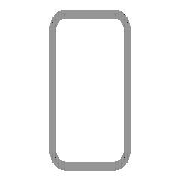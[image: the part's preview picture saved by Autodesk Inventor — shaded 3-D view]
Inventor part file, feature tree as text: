
AUTODESK INVENTOR PART (.ipt)
format: ipt  version: 2025 (Build 290162010, 162A)  size: 144,384 bytes
history: native  units: mm (DEFAULTED — no unit token found)
features: other x4, plane x2, split x1, sketch x1
ambient origin geometry x8: Origin, YZ Plane, XZ Plane, XY Plane, X Axis, Y Axis, Z Axis, Center Point
bodies: Solid1 (feature_tree), Body (feature_tree)
feature tree (8):
  parser-record x1  (decoder bookkeeping rows leaked as tree rows — omitted from the tree; the rows remain in map.json)
  other  "Driven Length"
  other  "Start Plane"
  other  "End Plane"
  plane  "Work Plane5"
  split  "Split2"
  sketch  "Sketch3"  dims[d3=173.0mm d4=0.0mm d7=4.0mm d9=20.0mm d11=40.0mm d12=2.0mm d13=40.0mm d14=213.0mm d15=10.0mm d16=20.0mm d17=90.0deg d18=173.0mm]
  plane  "Work Plane3"
